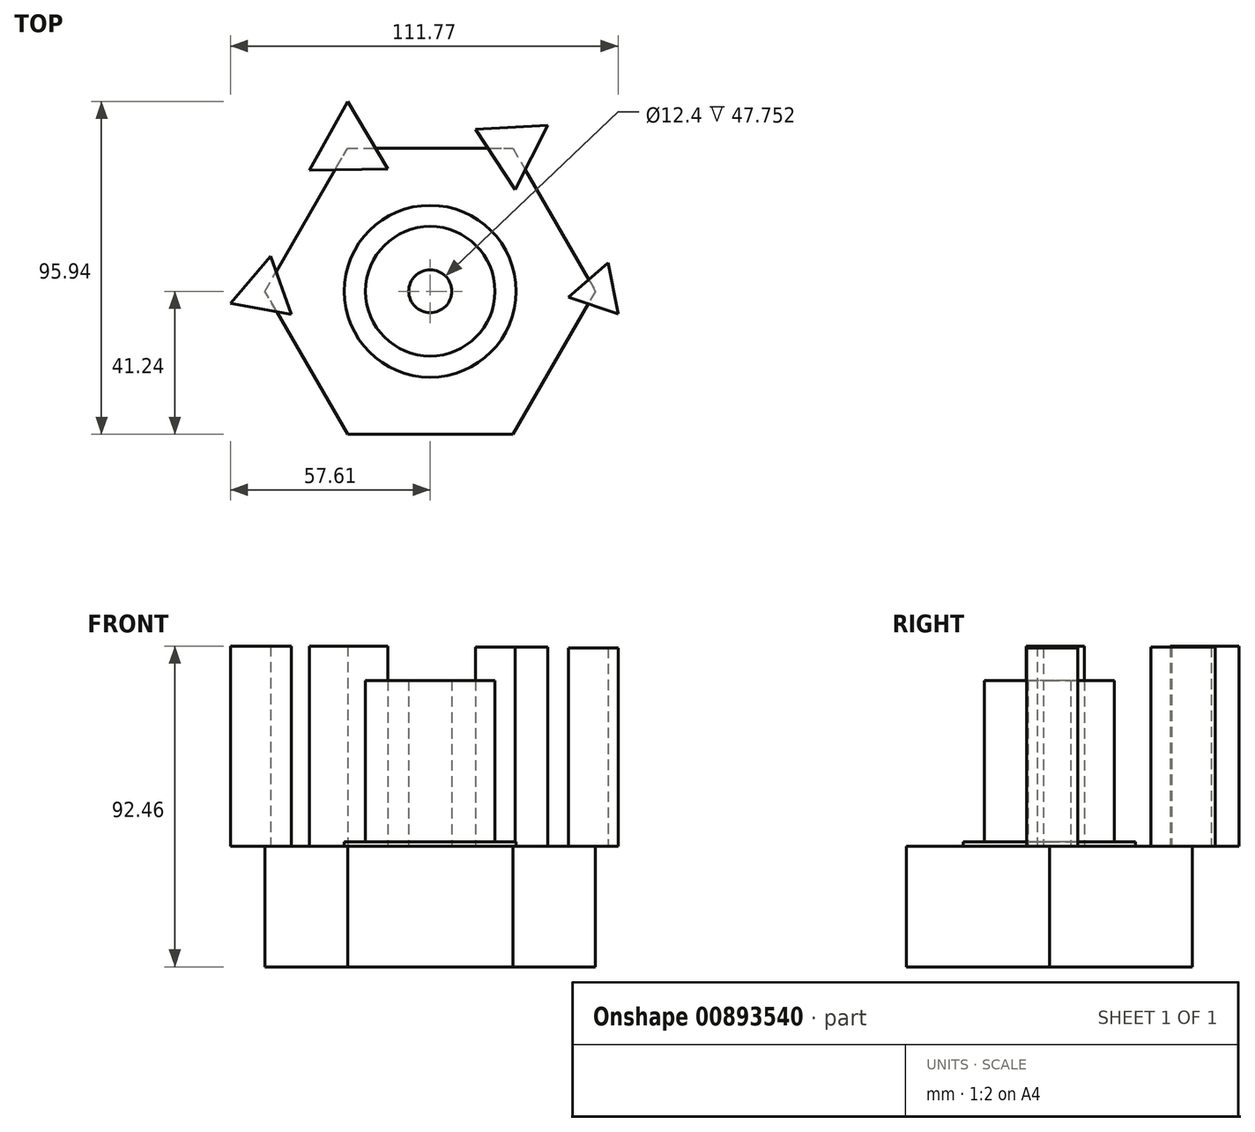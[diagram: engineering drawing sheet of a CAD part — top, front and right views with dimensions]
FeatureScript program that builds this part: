
annotation { "Feature Type Name" : "Feature", "Feature Type Description" : "" }
export const myFeature = defineFeature(function(context is Context, id is Id, definition is map)
    precondition{}
    {
        {
            var Q0;
            Q0=qCreatedBy(makeId("Top.planeOp"),FACE);
            var sketch = newSketch(context, id + "F0", { "sketchPlane" : qUnion([Q0])});
            skCircle(sketch, "E0.cCircle", {"center": v(0, 0) * mm, "radius": 43.8 * mm, "construction": true});
            skLineSegment(sketch, "E0.0", {"start": v(-50.58, 0.25) * mm, "end": v(-25.07, 43.93) * mm});
            skLineSegment(sketch, "E0.1", {"start": v(-25.07, 43.93) * mm, "end": v(25.5, 43.68) * mm});
            skLineSegment(sketch, "E0.2", {"start": v(25.5, 43.68) * mm, "end": v(50.58, -0.25) * mm});
            skLineSegment(sketch, "E0.3", {"start": v(50.58, -0.25) * mm, "end": v(25.07, -43.93) * mm});
            skLineSegment(sketch, "E0.4", {"start": v(25.07, -43.93) * mm, "end": v(-25.5, -43.68) * mm});
            skLineSegment(sketch, "E0.5", {"start": v(-25.5, -43.68) * mm, "end": v(-50.58, 0.25) * mm});
            skPoint(sketch, "E0.0.midPoint", {"position": v(-37.82, 22.09) * mm});
            skCircle(sketch, "E1", {"center": v(0, 0) * mm, "radius": 18.68 * mm});
            skCircle(sketch, "E2", {"center": v(0, 0) * mm, "radius": 6.2 * mm});
            skSolve(sketch);
        }
        {
            var Q0;
            Q0=makeQuery(id+"F0.imprint","IMPRINT",FACE,{"disambiguationData":[TD([[makeQuery(id+"F0.imprint","IMPRINT",EDGE,{"derivedFrom":sQuery(id+"F0.wireOp",EDGE,"E1")}),1.0]])]});
            extrude(context, id + "F1", {"entities" : qUnion([Q0]), "depth" : 47.75 * mm, "offsetDistance" : 25.4 * mm});
        }
        {
            var Q0;
            Q0=qCreatedBy(makeId("Top.planeOp"),FACE);
            var sketch = newSketch(context, id + "F2", { "sketchPlane" : qUnion([Q0])});
            skCircle(sketch, "E3.cCircle", {"center": v(0, 0) * mm, "radius": 41.24 * mm, "construction": true});
            skLineSegment(sketch, "E3.0", {"start": v(-23.8, 41.24) * mm, "end": v(23.8, 41.24) * mm});
            skLineSegment(sketch, "E3.1", {"start": v(23.8, 41.24) * mm, "end": v(47.62, 0) * mm});
            skLineSegment(sketch, "E3.2", {"start": v(47.62, 0) * mm, "end": v(23.8, -41.24) * mm});
            skLineSegment(sketch, "E3.3", {"start": v(23.8, -41.24) * mm, "end": v(-23.8, -41.24) * mm});
            skLineSegment(sketch, "E3.4", {"start": v(-23.8, -41.24) * mm, "end": v(-47.62, 0) * mm});
            skLineSegment(sketch, "E3.5", {"start": v(-47.62, 0) * mm, "end": v(-23.8, 41.24) * mm});
            skPoint(sketch, "E3.0.midPoint", {"position": v(0, 41.24) * mm});
            skSolve(sketch);
        }
        {
            var Q0;
            Q0=makeQuery(id+"F2.imprint","IMPRINT",FACE,{"disambiguationData":[TD([[makeQuery(id+"F2.imprint","IMPRINT",EDGE,{"derivedFrom":sQuery(id+"F2.wireOp",EDGE,"E3.0")}),-1.0]])]});
            extrude(context, id + "F3", {"entities" : qUnion([Q0]), "operationType" : NewBodyOperationType.ADD, "oppositeDirection" : true, "depth" : 34.8 * mm, "offsetDistance" : 25.4 * mm});
        }
        {
            var Q0;
            Q0=qCreatedBy(makeId("Top.planeOp"),FACE);
            var sketch = newSketch(context, id + "F4", { "sketchPlane" : qUnion([Q0])});
            skCircle(sketch, "E4", {"center": v(0, 0) * mm, "radius": 12.65 * mm});
            skCircle(sketch, "E5", {"center": v(0, 0) * mm, "radius": 24.77 * mm});
            skSolve(sketch);
        }
        {
            var Q0;
            Q0=makeQuery(id+"F4.imprint","IMPRINT",FACE,{"disambiguationData":[TD([[makeQuery(id+"F4.imprint","IMPRINT",EDGE,{"derivedFrom":sQuery(id+"F4.wireOp",EDGE,"E4")}),-1.0]])]});
            extrude(context, id + "F5", {"entities" : qUnion([Q0]), "operationType" : NewBodyOperationType.ADD, "depth" : 1.27 * mm, "offsetDistance" : 25.4 * mm});
        }
        {
            var Q0;
            Q0=qCreatedBy(makeId("Top.planeOp"),FACE);
            var sketch = newSketch(context, id + "F6", { "sketchPlane" : qUnion([Q0])});
            skCircle(sketch, "E6.cCircle", {"center": v(-23.6, 41.62) * mm, "radius": 13.08 * mm, "construction": true});
            skLineSegment(sketch, "E6.0", {"start": v(-23.8, 54.7) * mm, "end": v(-12.18, 35.24) * mm});
            skLineSegment(sketch, "E6.1", {"start": v(-12.18, 35.24) * mm, "end": v(-34.84, 34.91) * mm});
            skLineSegment(sketch, "E6.2", {"start": v(-34.84, 34.91) * mm, "end": v(-23.8, 54.7) * mm});
            skSolve(sketch);
        }
        {
            var Q0;
            Q0=makeQuery(id+"F6.imprint","IMPRINT",FACE,{"disambiguationData":[TD([[makeQuery(id+"F6.imprint","IMPRINT",EDGE,{"derivedFrom":sQuery(id+"F6.wireOp",EDGE,"E6.0")}),-1.0]])]});
            extrude(context, id + "F7", {"entities" : qUnion([Q0]), "operationType" : NewBodyOperationType.ADD, "depth" : 57.66 * mm, "offsetDistance" : 25.4 * mm});
        }
        {
            var Q0;
            Q0=qCreatedBy(makeId("Top.planeOp"),FACE);
            var sketch = newSketch(context, id + "F8", { "sketchPlane" : qUnion([Q0])});
            skCircle(sketch, "E7.cCircle", {"center": v(23.8, 41.24) * mm, "radius": 12.04 * mm, "construction": true});
            skLineSegment(sketch, "E7.0", {"start": v(33.84, 47.87) * mm, "end": v(24.52, 29.22) * mm});
            skLineSegment(sketch, "E7.1", {"start": v(24.52, 29.22) * mm, "end": v(13.02, 46.62) * mm});
            skLineSegment(sketch, "E7.2", {"start": v(13.02, 46.62) * mm, "end": v(33.84, 47.87) * mm});
            skSolve(sketch);
        }
        {
            var Q0;
            Q0=makeQuery(id+"F8.imprint","IMPRINT",FACE,{"disambiguationData":[TD([[makeQuery(id+"F8.imprint","IMPRINT",EDGE,{"derivedFrom":sQuery(id+"F8.wireOp",EDGE,"E7.0")}),-1.0]])]});
            extrude(context, id + "F9", {"entities" : qUnion([Q0]), "operationType" : NewBodyOperationType.ADD, "depth" : 57.4 * mm, "offsetDistance" : 25.4 * mm});
        }
        {
            var Q0;
            Q0=qCreatedBy(makeId("Top.planeOp"),FACE);
            var sketch = newSketch(context, id + "F10", { "sketchPlane" : qUnion([Q0])});
            skCircle(sketch, "E8.cCircle", {"center": v(-47.87, 0) * mm, "radius": 10.32 * mm, "construction": true});
            skLineSegment(sketch, "E8.0", {"start": v(-45.98, 10.14) * mm, "end": v(-40.04, -6.71) * mm});
            skLineSegment(sketch, "E8.1", {"start": v(-40.04, -6.71) * mm, "end": v(-57.6, -3.43) * mm});
            skLineSegment(sketch, "E8.2", {"start": v(-57.6, -3.43) * mm, "end": v(-45.98, 10.14) * mm});
            skSolve(sketch);
        }
        {
            var Q0;
            Q0=makeQuery(id+"F10.imprint","IMPRINT",FACE,{"disambiguationData":[TD([[makeQuery(id+"F10.imprint","IMPRINT",EDGE,{"derivedFrom":sQuery(id+"F10.wireOp",EDGE,"E8.0")}),-1.0]])]});
            extrude(context, id + "F11", {"entities" : qUnion([Q0]), "operationType" : NewBodyOperationType.ADD, "depth" : 57.66 * mm, "offsetDistance" : 25.4 * mm});
        }
        {
            var Q0;
            Q0=qCreatedBy(makeId("Top.planeOp"),FACE);
            var sketch = newSketch(context, id + "F12", { "sketchPlane" : qUnion([Q0])});
            skCircle(sketch, "E9.cCircle", {"center": v(48.44, 0) * mm, "radius": 8.72 * mm, "construction": true});
            skLineSegment(sketch, "E9.0", {"start": v(51.29, 8.25) * mm, "end": v(54.16, -6.59) * mm});
            skLineSegment(sketch, "E9.1", {"start": v(54.16, -6.59) * mm, "end": v(39.88, -1.66) * mm});
            skLineSegment(sketch, "E9.2", {"start": v(39.88, -1.66) * mm, "end": v(51.29, 8.25) * mm});
            skSolve(sketch);
        }
        {
            var Q0;
            Q0=makeQuery(id+"F12.imprint","IMPRINT",FACE,{"disambiguationData":[TD([[makeQuery(id+"F12.imprint","IMPRINT",EDGE,{"derivedFrom":sQuery(id+"F12.wireOp",EDGE,"E9.0")}),-1.0]])]});
            extrude(context, id + "F13", {"entities" : qUnion([Q0]), "operationType" : NewBodyOperationType.ADD, "depth" : 57.15 * mm, "offsetDistance" : 25.4 * mm});
        }
    });
